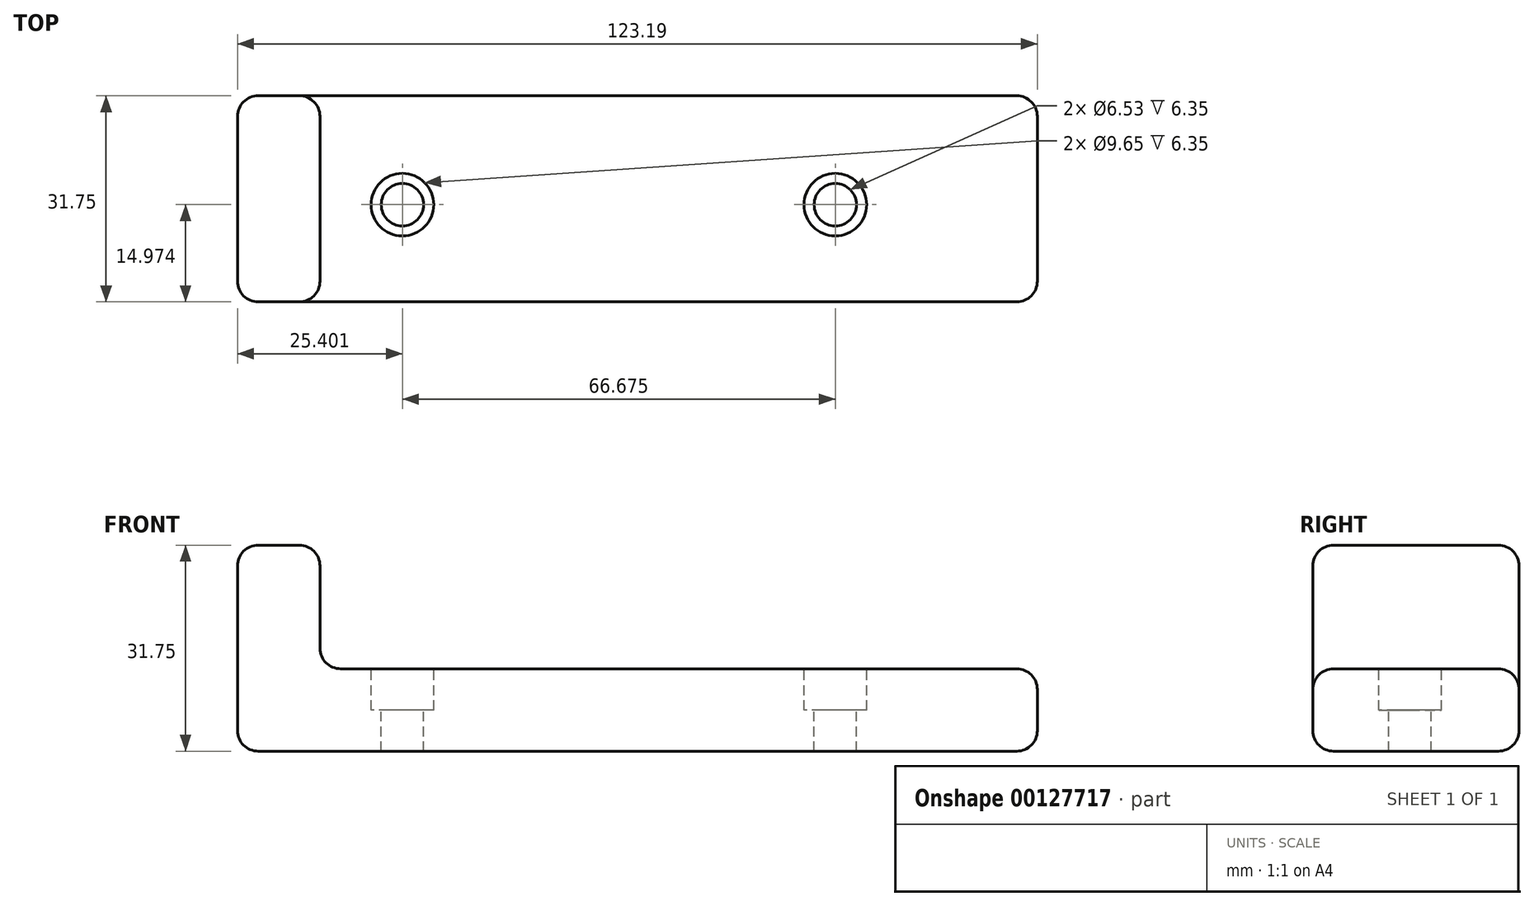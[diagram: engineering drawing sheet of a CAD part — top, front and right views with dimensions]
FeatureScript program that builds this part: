
annotation { "Feature Type Name" : "Feature", "Feature Type Description" : "" }
export const myFeature = defineFeature(function(context is Context, id is Id, definition is map)
    precondition{}
    {
        {
            var Q0;
            Q0=qCreatedBy(makeId("Front.planeOp"),FACE);
            var sketch = newSketch(context, id + "F0", { "sketchPlane" : qUnion([Q0])});
            skLineSegment(sketch, "E0", {"start": v(-58.25, 22.8) * mm, "end": v(-45.55, 22.8) * mm});
            skLineSegment(sketch, "E1", {"start": v(-45.55, 22.8) * mm, "end": v(-45.55, 6.92) * mm});
            skLineSegment(sketch, "E2", {"start": v(-42.37, 3.74) * mm, "end": v(64.94, 3.74) * mm});
            skLineSegment(sketch, "E3", {"start": v(64.94, 3.74) * mm, "end": v(64.94, -8.96) * mm});
            skLineSegment(sketch, "E4", {"start": v(64.94, -8.96) * mm, "end": v(-58.25, -8.96) * mm});
            skLineSegment(sketch, "E5", {"start": v(-58.25, -8.96) * mm, "end": v(-58.25, 22.8) * mm});
            skPoint(sketch, "E6.visualSharp", {"position": v(-45.55, 3.74) * mm});
            skArc(sketch, "E6.filletArc", {"start": v(-45.55, 6.92) * mm, "mid": v(-44.62, 4.67) * mm, "end": v(-42.37, 3.74) * mm});
            skSolve(sketch);
        }
        {
            var Q0;
            Q0 = qSketchRegion(id + "F0", true);
            extrude(context, id + "F1", {"entities" : qUnion([Q0]), "depth" : 31.75 * mm});
        }
        {
            var Q0;
            Q0=makeQuery(id+"F1.opExtrude","CAP_EDGE",EDGE,{"disambiguationData":[OSD([sQuery(id+"F0.wireOp",EDGE,"E3")])],"isStart":true});
            var Q1;
            Q1=makeQuery(id+"F1.opExtrude","CAP_FACE",FACE,{"disambiguationData":[OSD([sQuery(id+"F0.wireOp",EDGE,"E0"),sQuery(id+"F0.wireOp",EDGE,"E1"),sQuery(id+"F0.wireOp",EDGE,"E2"),sQuery(id+"F0.wireOp",EDGE,"E3"),sQuery(id+"F0.wireOp",EDGE,"E4"),sQuery(id+"F0.wireOp",EDGE,"E5"),sQuery(id+"F0.wireOp",EDGE,"E6.filletArc")])],"isStart":true});
            fillet(context, id + "F2", {"entities" : qUnion([Q0, Q1]), "radius" : 3.17 * mm, "tangentPropagation" : true, "allowEdgeOverflow" : false});
        }
        {
            var Q0;
            Q0=makeQuery(id+"F1.opExtrude","CAP_EDGE",EDGE,{"disambiguationData":[OSD([sQuery(id+"F0.wireOp",EDGE,"E0")])],"isStart":false});
            var Q1;
            Q1=makeQuery(id+"F1.opExtrude","SWEPT_EDGE",EDGE,{"disambiguationData":[OSD([sQuery(id+"F0.wireOp",EDGE,"E0"),sQuery(id+"F0.wireOp",EDGE,"E5")])]});
            var Q2;
            Q2=makeQuery(id+"F1.opExtrude","SWEPT_EDGE",EDGE,{"disambiguationData":[OSD([sQuery(id+"F0.wireOp",EDGE,"E0"),sQuery(id+"F0.wireOp",EDGE,"E1")])]});
            var Q3;
            Q3=makeQuery(id+"F1.opExtrude","CAP_EDGE",EDGE,{"disambiguationData":[OSD([sQuery(id+"F0.wireOp",EDGE,"E5")])],"isStart":false});
            var Q4;
            Q4=makeQuery(id+"F1.opExtrude","CAP_FACE",FACE,{"disambiguationData":[OSD([sQuery(id+"F0.wireOp",EDGE,"E0"),sQuery(id+"F0.wireOp",EDGE,"E1"),sQuery(id+"F0.wireOp",EDGE,"E2"),sQuery(id+"F0.wireOp",EDGE,"E3"),sQuery(id+"F0.wireOp",EDGE,"E4"),sQuery(id+"F0.wireOp",EDGE,"E5"),sQuery(id+"F0.wireOp",EDGE,"E6.filletArc")])],"isStart":false});
            var Q5;
            Q5=makeQuery(id+"F1.opExtrude","CAP_EDGE",EDGE,{"disambiguationData":[OSD([sQuery(id+"F0.wireOp",EDGE,"E4")])],"isStart":false});
            var Q6;
            Q6=makeQuery(id+"F1.opExtrude","SWEPT_EDGE",EDGE,{"disambiguationData":[OSD([sQuery(id+"F0.wireOp",EDGE,"E2"),sQuery(id+"F0.wireOp",EDGE,"E3")])]});
            var Q7;
            Q7=makeQuery(id+"F1.opExtrude","SWEPT_EDGE",EDGE,{"disambiguationData":[OSD([sQuery(id+"F0.wireOp",EDGE,"E3"),sQuery(id+"F0.wireOp",EDGE,"E4")])]});
            fillet(context, id + "F3", {"entities" : qUnion([Q0, Q1, Q2, Q3, Q4, Q5, Q6, Q7]), "radius" : 3.17 * mm, "tangentPropagation" : true, "allowEdgeOverflow" : false});
        }
        {
            var Q0;
            Q0=makeQuery(id+"F1.opExtrude","SWEPT_FACE",FACE,{"disambiguationData":[OSD([sQuery(id+"F0.wireOp",EDGE,"E5")])]});
            fillet(context, id + "F4", {"entities" : qUnion([Q0]), "radius" : 3.17 * mm, "tangentPropagation" : true, "allowEdgeOverflow" : false});
        }
        {
            var Q0;
            Q0=makeQuery(id+"F1.opExtrude","SWEPT_FACE",FACE,{"disambiguationData":[OSD([sQuery(id+"F0.wireOp",EDGE,"E2")])]});
            var sketch = newSketch(context, id + "F5", { "sketchPlane" : qUnion([Q0])});
            skCircle(sketch, "E7", {"center": v(-32.85, -16.78) * mm, "radius": 4.83 * mm});
            skCircle(sketch, "E8", {"center": v(33.83, -16.78) * mm, "radius": 4.83 * mm});
            skArc(sketch, "E9", {"start": v(6.6, -13.64) * mm, "mid": v(5.63, -16.81) * mm, "end": v(6.6, -19.99) * mm});
            skArc(sketch, "E10", {"start": v(14.2, -19.99) * mm, "mid": v(15.16, -16.81) * mm, "end": v(14.2, -13.64) * mm});
            skLineSegment(sketch, "E11", {"start": v(6.6, -13.64) * mm, "end": v(14.2, -13.64) * mm});
            skLineSegment(sketch, "E12", {"start": v(6.6, -19.99) * mm, "end": v(14.2, -19.99) * mm});
            skSolve(sketch);
        }
        {
            var Q0;
            Q0=sQuery(id+"F5.wireOp",VERTEX,"E8.center");
            var Q1;
            Q1=makeQuery(id+"F1.opExtrude","SWEPT_BODY",BODY,{"disambiguationData":[OSD([sQuery(id+"F0.wireOp",EDGE,"E0"),sQuery(id+"F0.wireOp",EDGE,"E1"),sQuery(id+"F0.wireOp",EDGE,"E2"),sQuery(id+"F0.wireOp",EDGE,"E3"),sQuery(id+"F0.wireOp",EDGE,"E4"),sQuery(id+"F0.wireOp",EDGE,"E5"),sQuery(id+"F0.wireOp",EDGE,"E6.filletArc")])]});
            hole(context, id + "F6", {"style" : HoleStyle.C_BORE, "endStyle" : HoleEndStyle.THROUGH, "holeDiameter" : 6.53 * mm, "cBoreDiameter" : 9.65 * mm, "cBoreDepth" : 6.35 * mm, "startFromSketch" : true, "locations" : qUnion([Q0]), "scope" : qUnion([Q1]), "isTappedThrough" : true});
        }
        {
            var Q0;
            Q0=sQuery(id+"F5.wireOp",VERTEX,"E7.center");
            var Q1;
            Q1=makeQuery(id+"F1.opExtrude","SWEPT_BODY",BODY,{"disambiguationData":[OSD([sQuery(id+"F0.wireOp",EDGE,"E0"),sQuery(id+"F0.wireOp",EDGE,"E1"),sQuery(id+"F0.wireOp",EDGE,"E2"),sQuery(id+"F0.wireOp",EDGE,"E3"),sQuery(id+"F0.wireOp",EDGE,"E4"),sQuery(id+"F0.wireOp",EDGE,"E5"),sQuery(id+"F0.wireOp",EDGE,"E6.filletArc")])]});
            hole(context, id + "F7", {"style" : HoleStyle.C_BORE, "endStyle" : HoleEndStyle.THROUGH, "holeDiameter" : 6.53 * mm, "cBoreDiameter" : 9.65 * mm, "cBoreDepth" : 6.35 * mm, "startFromSketch" : true, "locations" : qUnion([Q0]), "scope" : qUnion([Q1]), "isTappedThrough" : true});
        }
        {
            var Q0;
            Q0=sQuery(id+"F5.wireOp",EDGE,"E9");
            var Q1;
            Q1=sQuery(id+"F5.wireOp",EDGE,"E12");
            var Q2;
            Q2=sQuery(id+"F5.wireOp",EDGE,"E10");
            var Q3;
            Q3=sQuery(id+"F5.wireOp",EDGE,"E11");
            extrude(context, id + "F8", {"bodyType" : ToolBodyType.SURFACE, "operationType" : NewBodyOperationType.INTERSECT, "surfaceEntities" : qUnion([Q0, Q1, Q2, Q3]), "oppositeDirection" : true, "depth" : 12.95 * mm});
        }
        {
            var Q0;
            Q0=makeQuery(id+"F1.opExtrude","SWEPT_FACE",FACE,{"disambiguationData":[OSD([sQuery(id+"F0.wireOp",EDGE,"E5")])]});
            var sketch = newSketch(context, id + "F9", { "sketchPlane" : qUnion([Q0])});
            skCircle(sketch, "E13", {"center": v(15.88, 6.92) * mm, "radius": 12.7 * mm});
            skSolve(sketch);
        }
        {
            var Q0;
            Q0=sQuery(id+"F9.wireOp",EDGE,"E13");
            extrude(context, id + "F10", {"bodyType" : ToolBodyType.SURFACE, "surfaceEntities" : qUnion([Q0]), "depth" : 25.4 * mm});
        }
    });
